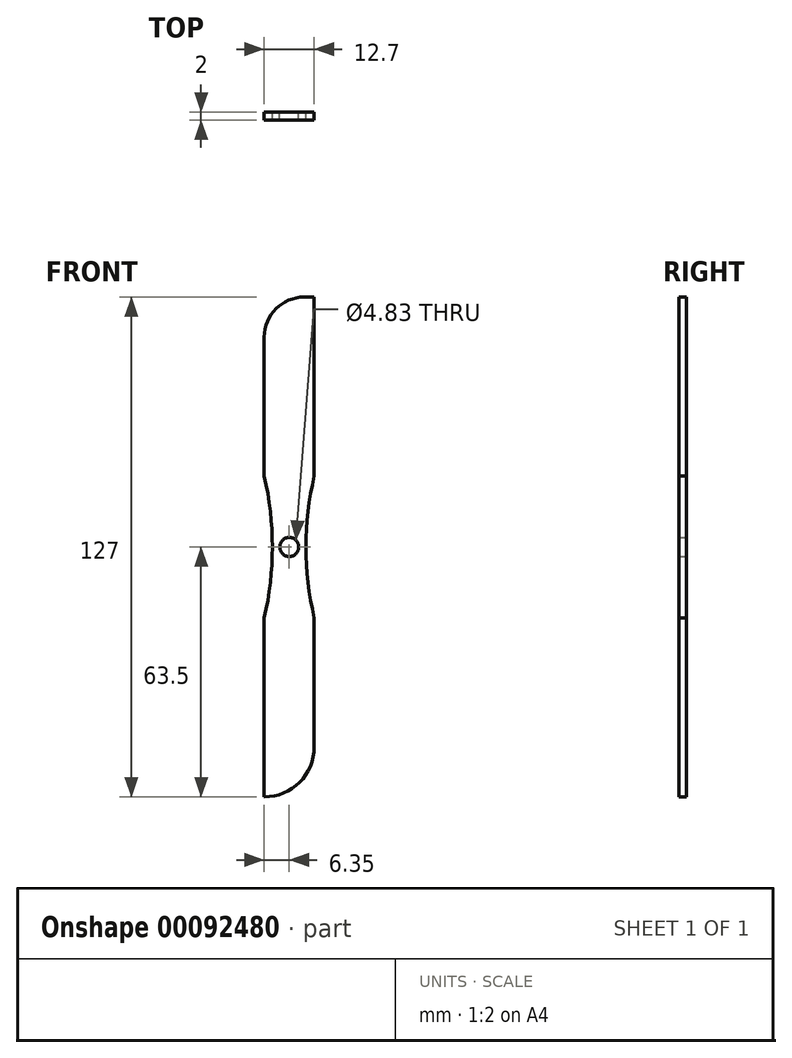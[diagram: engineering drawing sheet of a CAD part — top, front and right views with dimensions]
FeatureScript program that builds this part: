
annotation { "Feature Type Name" : "Feature", "Feature Type Description" : "" }
export const myFeature = defineFeature(function(context is Context, id is Id, definition is map)
    precondition{}
    {
        {
            var Q0;
            Q0=qCreatedBy(makeId("Front.planeOp"),FACE);
            var sketch = newSketch(context, id + "F0", { "sketchPlane" : qUnion([Q0])});
            skLineSegment(sketch, "E0.bottom", {"start": v(-6.35, -63.5) * mm, "end": v(-6.35, -63.5) * mm});
            skLineSegment(sketch, "E0.top", {"start": v(3.81, 63.5) * mm, "end": v(6.35, 63.5) * mm});
            skLineSegment(sketch, "E0.left", {"start": v(-6.35, -63.5) * mm, "end": v(-6.35, -18) * mm});
            skLineSegment(sketch, "E0.right", {"start": v(6.35, -50.8) * mm, "end": v(6.35, -18) * mm});
            skPoint(sketch, "E0.middle", {"position": v(0, 0) * mm});
            skCircle(sketch, "E1", {"center": v(0, 0) * mm, "radius": 2.41 * mm});
            skLineSegment(sketch, "E2.bottom", {"start": v(-6.8, -18) * mm, "end": v(6.8, -18) * mm, "construction": true});
            skLineSegment(sketch, "E2.top", {"start": v(-6.8, 18) * mm, "end": v(6.8, 18) * mm, "construction": true});
            skLineSegment(sketch, "E2.left", {"start": v(-6.8, -18) * mm, "end": v(-6.8, 18) * mm, "construction": true});
            skLineSegment(sketch, "E2.right", {"start": v(6.8, -18) * mm, "end": v(6.8, 18) * mm, "construction": true});
            skArc(sketch, "E3", {"start": v(6.35, 18) * mm, "mid": v(4.28, 0) * mm, "end": v(6.35, -18) * mm});
            skArc(sketch, "E4", {"start": v(-6.35, -18) * mm, "mid": v(-4.28, 0) * mm, "end": v(-6.35, 18) * mm});
            skLineSegment(sketch, "E5.trimOffspring", {"start": v(-6.35, 18) * mm, "end": v(-6.35, 53.34) * mm});
            skLineSegment(sketch, "E6.trimOffspring", {"start": v(6.35, 18) * mm, "end": v(6.35, 63.5) * mm});
            skPoint(sketch, "E7.visualSharp", {"position": v(-6.35, 63.5) * mm});
            skArc(sketch, "E7.filletArc", {"start": v(3.81, 63.5) * mm, "mid": v(-3.37, 60.52) * mm, "end": v(-6.35, 53.34) * mm});
            skPoint(sketch, "E8.visualSharp", {"position": v(6.35, -63.5) * mm});
            skArc(sketch, "E8.filletArc", {"start": v(-6.35, -63.5) * mm, "mid": v(2.63, -59.78) * mm, "end": v(6.35, -50.8) * mm});
            skSolve(sketch);
        }
        {
            var Q0;
            Q0=makeQuery(id+"F0.imprint","IMPRINT",FACE,{"disambiguationData":[TD([[makeQuery(id+"F0.imprint","IMPRINT",EDGE,{"derivedFrom":sQuery(id+"F0.wireOp",EDGE,"E0.top")}),-1.0]])]});
            extrude(context, id + "F1", {"entities" : qUnion([Q0]), "depth" : 2 * mm});
        }
    });
